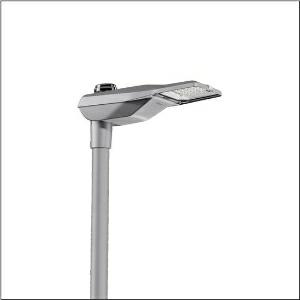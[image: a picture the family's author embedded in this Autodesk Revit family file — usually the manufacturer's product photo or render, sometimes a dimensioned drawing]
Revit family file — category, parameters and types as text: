
# Revit family: streetlight_sl_21_micro___pl52_5xe5h37n08cb_9265
name_source: partatom
category: Lighting Fixtures
units: mm (PartAtom-declared; Revit-internal decimal feet)

## family parameters
Cut with Voids When Loaded = No
Host = Face
Light Source = No
Part Type = Normal
Room Calculation Point = No
Round Connector Dimension = Use Diameter
Shared = No

## types (1)
- --- (1 x LED, 2250 lm, 15.8 W, 3000K)
    Apparent Load = 16 VA
    CIE Flux Codes = 27 59 98 100 100
    Color Rendering = 70
    Color Temperature = 3000K
    Default Elevation = 1800 mm
    Description = Streetlight SL 21 micro, mast luminaire, primary light control with lens, of PMMA, primary optical cover: cover, of toughened safety glass, transparent, light distribution: PL52, light emission: direct distribution, primary light characteristic: asymmetric, installation type: post-top, LED, 3G 1.5mm², High Power LED, rated luminous flux: 2.250lm, luminous efficacy: 142lm/W, light colour: 730, colour temperature: 3000K, control gear: NEMA (7pin), control: overheat protection, pre-setting: linear dimming characteristic, constant luminous flux control, time-dependent luminous flux control, flexible luminous flux parameterisation, mains connection: 230..240V, AC, 50/60Hz, connection cable pre-assembled, cable length: 6,5m, wiring characteristics: H07RN-F, start of lifetime: 16W, end of service life: 16W, reduction: 8W, luminaire housing, of diecast aluminium (EN AC-44300), powder-coated, Siteco® metallic grey (DB 702S), corrosivity category C5 mid according to DIN EN ISO 12944, multi-level sealing system, sealing non-destructively replaceable, inclination adjustable: 0°, 5°, 10°, 15°, length: 528mm, width: 235mm, height: 110mm, spigot size: 76/60mm (post-top), mounting height: 4..8m, protection rating (complete): IP66, insulation class (complete): insulation class I (protective earthing), certification: CE, ENEC, ENEC+, VDE, impact resistance: IK10, permissible operating ambient temperature for outdoor applications: -40..+50°C, standard-compliant lighting for roads and squares, packaging unit: 1 piece

Light Distribution: PL52
    Height = 110 mm
    Lamp = 1 x LED
    Lamp Light Flux = 2250 lm
    Lamp Power = 15.8 W
    Lamp count = 1
    Length = 528 mm
    Luminous efficacy = 142 lm/W
    Manufacturer = Siteco
    ModVariant = No
    Model = 5XE5H37N08CB
    Number of Poles = 1
    OnlyDefault = Yes
    Power Factor = 1
    Product Name = Streetlight SL 21 micro | PL52
    Product group = mast luminaire | pylon top
    ProductGroupID = 6100
    Protection Class = Protection class I
    Protection Degree = IP 66
    RLX_Detail_Level = 1
    RLX_Emergency_Light_Flux = 0 lm
    RLX_Emergency_Type = 0
    RLX_Emergency_Type_DB = No
    RlxData = <blob elided: 108149 chars, md5=96257941>
    Socket = socket
    Standby Power = 0 W
    System Light Flux = 2250 lm
    System Power = 16 W
    Type Comments = factory setting: luminous flux: 100 % | dim-lin: 254 | 300 mA
    Type Image = l_1294375.jpg
    URL = http://relux.com
    VarID = @adj_158709
    Voltage = 0 V
    Weight = 0.00 kg
    Width = 235 mm

## geometry (parser evidence)
native form markers: Blend x4, Sweep x9
no freeform markers — native parametric forms only
